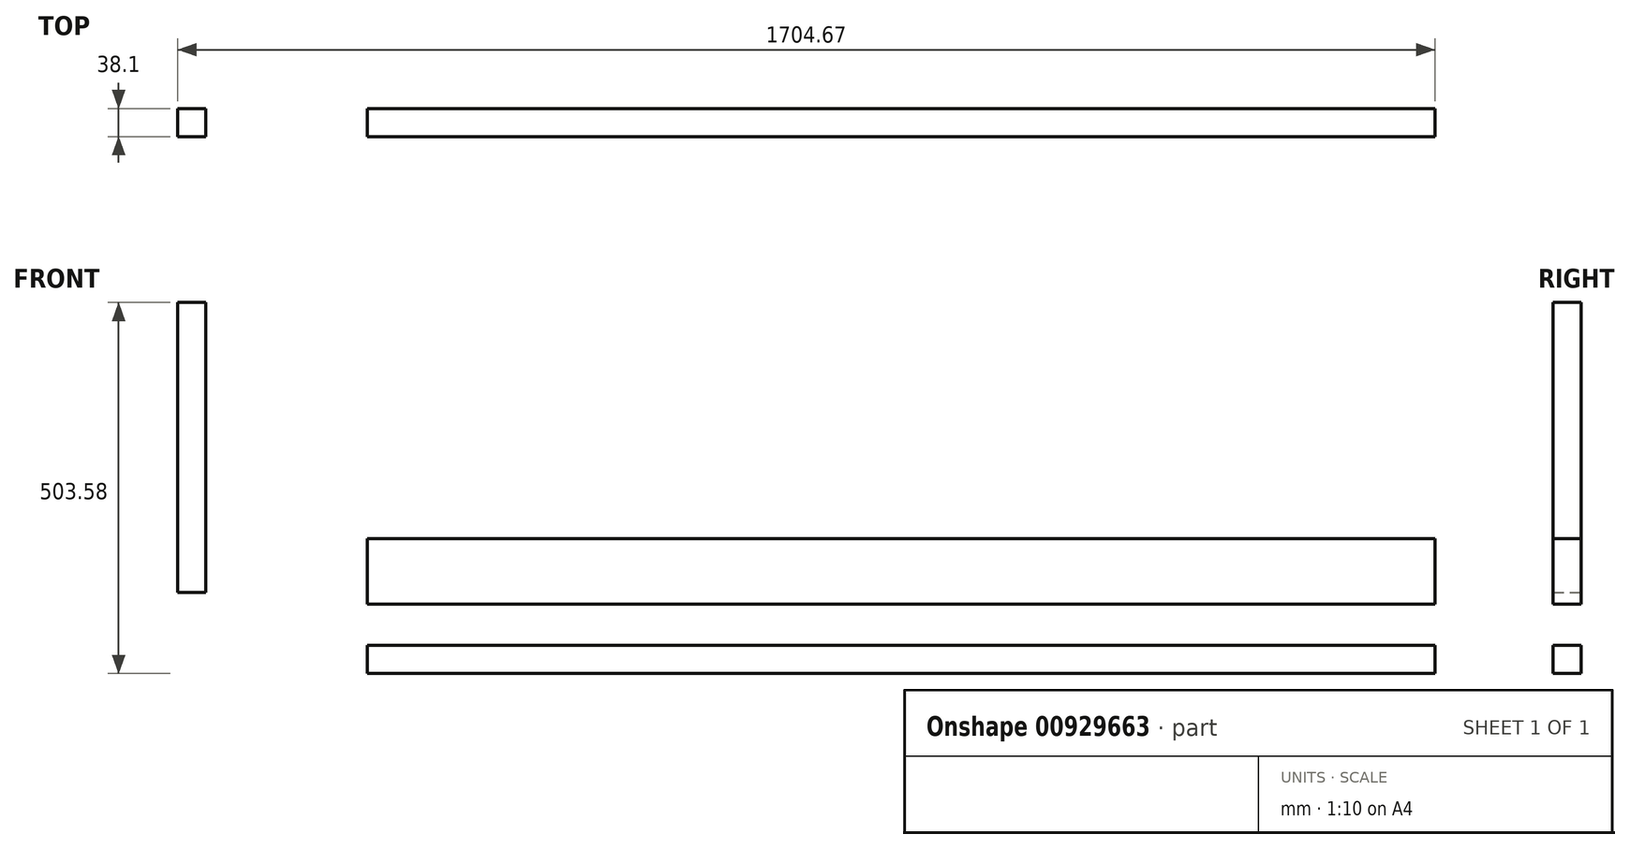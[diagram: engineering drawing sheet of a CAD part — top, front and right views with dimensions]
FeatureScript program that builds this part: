
annotation { "Feature Type Name" : "Feature", "Feature Type Description" : "" }
export const myFeature = defineFeature(function(context is Context, id is Id, definition is map)
    precondition{}
    {
        {
            var Q0;
            Q0=qCreatedBy(makeId("Front.planeOp"),FACE);
            var sketch = newSketch(context, id + "F0", { "sketchPlane" : qUnion([Q0])});
            skLineSegment(sketch, "E0.bottom", {"start": v(723.9, 44.45) * mm, "end": v(-723.9, 44.45) * mm});
            skLineSegment(sketch, "E0.top", {"start": v(723.9, -44.45) * mm, "end": v(-723.9, -44.45) * mm});
            skLineSegment(sketch, "E0.left", {"start": v(723.9, 44.45) * mm, "end": v(723.9, -44.45) * mm});
            skLineSegment(sketch, "E0.right", {"start": v(-723.9, 44.45) * mm, "end": v(-723.9, -44.45) * mm});
            skPoint(sketch, "E0.middle", {"position": v(0, 0) * mm});
            skSolve(sketch);
        }
        {
            var Q0;
            Q0=makeQuery(id+"F0.imprint","IMPRINT",FACE,{"disambiguationData":[TD([[makeQuery(id+"F0.imprint","IMPRINT",EDGE,{"derivedFrom":sQuery(id+"F0.wireOp",EDGE,"E0.bottom")}),1.0]])]});
            extrude(context, id + "F1", {"entities" : qUnion([Q0]), "depth" : 38.1 * mm, "offsetDistance" : 25.4 * mm});
        }
        {
            var Q0;
            Q0=qCreatedBy(makeId("Front.planeOp"),FACE);
            var sketch = newSketch(context, id + "F2", { "sketchPlane" : qUnion([Q0])});
            skLineSegment(sketch, "E1.bottom", {"start": v(723.9, -138.28) * mm, "end": v(-723.9, -138.28) * mm});
            skLineSegment(sketch, "E1.top", {"start": v(723.9, -100.18) * mm, "end": v(-723.9, -100.18) * mm});
            skLineSegment(sketch, "E1.left", {"start": v(723.9, -138.28) * mm, "end": v(723.9, -100.18) * mm});
            skLineSegment(sketch, "E1.right", {"start": v(-723.9, -138.28) * mm, "end": v(-723.9, -100.18) * mm});
            skPoint(sketch, "E1.middle", {"position": v(0, -119.23) * mm});
            skSolve(sketch);
        }
        {
            var Q0;
            Q0=makeQuery(id+"F2.imprint","IMPRINT",FACE,{"disambiguationData":[TD([[makeQuery(id+"F2.imprint","IMPRINT",EDGE,{"derivedFrom":sQuery(id+"F2.wireOp",EDGE,"E1.bottom")}),-1.0]])]});
            extrude(context, id + "F3", {"entities" : qUnion([Q0]), "depth" : 38.1 * mm, "offsetDistance" : 25.4 * mm});
        }
        {
            var Q0;
            Q0=qCreatedBy(makeId("Front.planeOp"),FACE);
            var sketch = newSketch(context, id + "F4", { "sketchPlane" : qUnion([Q0])});
            skLineSegment(sketch, "E2.bottom", {"start": v(-942.67, -28.4) * mm, "end": v(-980.77, -28.4) * mm});
            skLineSegment(sketch, "E2.top", {"start": v(-942.67, 365.3) * mm, "end": v(-980.77, 365.3) * mm});
            skLineSegment(sketch, "E2.left", {"start": v(-942.67, -28.4) * mm, "end": v(-942.67, 365.3) * mm});
            skLineSegment(sketch, "E2.right", {"start": v(-980.77, -28.4) * mm, "end": v(-980.77, 365.3) * mm});
            skPoint(sketch, "E2.middle", {"position": v(-961.72, 168.45) * mm});
            skSolve(sketch);
        }
        {
            var Q0;
            Q0=makeQuery(id+"F4.imprint","IMPRINT",FACE,{"disambiguationData":[TD([[makeQuery(id+"F4.imprint","IMPRINT",EDGE,{"derivedFrom":sQuery(id+"F4.wireOp",EDGE,"E2.bottom")}),-1.0]])]});
            extrude(context, id + "F5", {"entities" : qUnion([Q0]), "depth" : 38.1 * mm, "offsetDistance" : 25.4 * mm});
        }
    });
